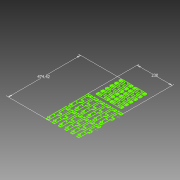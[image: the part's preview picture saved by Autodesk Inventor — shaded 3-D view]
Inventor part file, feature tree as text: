
AUTODESK INVENTOR PART (.ipt)
format: ipt  version: 2012 (Build 160160000, 160)  size: 196,096 bytes
history: native  units: mm
features: sketch x1
ambient origin geometry x8: Origin, YZ Plane, XZ Plane, XY Plane, X Axis, Y Axis, Z Axis, Center Point
feature tree (1):
  sketch  "Sketch1"  dims[d51=474.42021mm d52=230.0mm]
